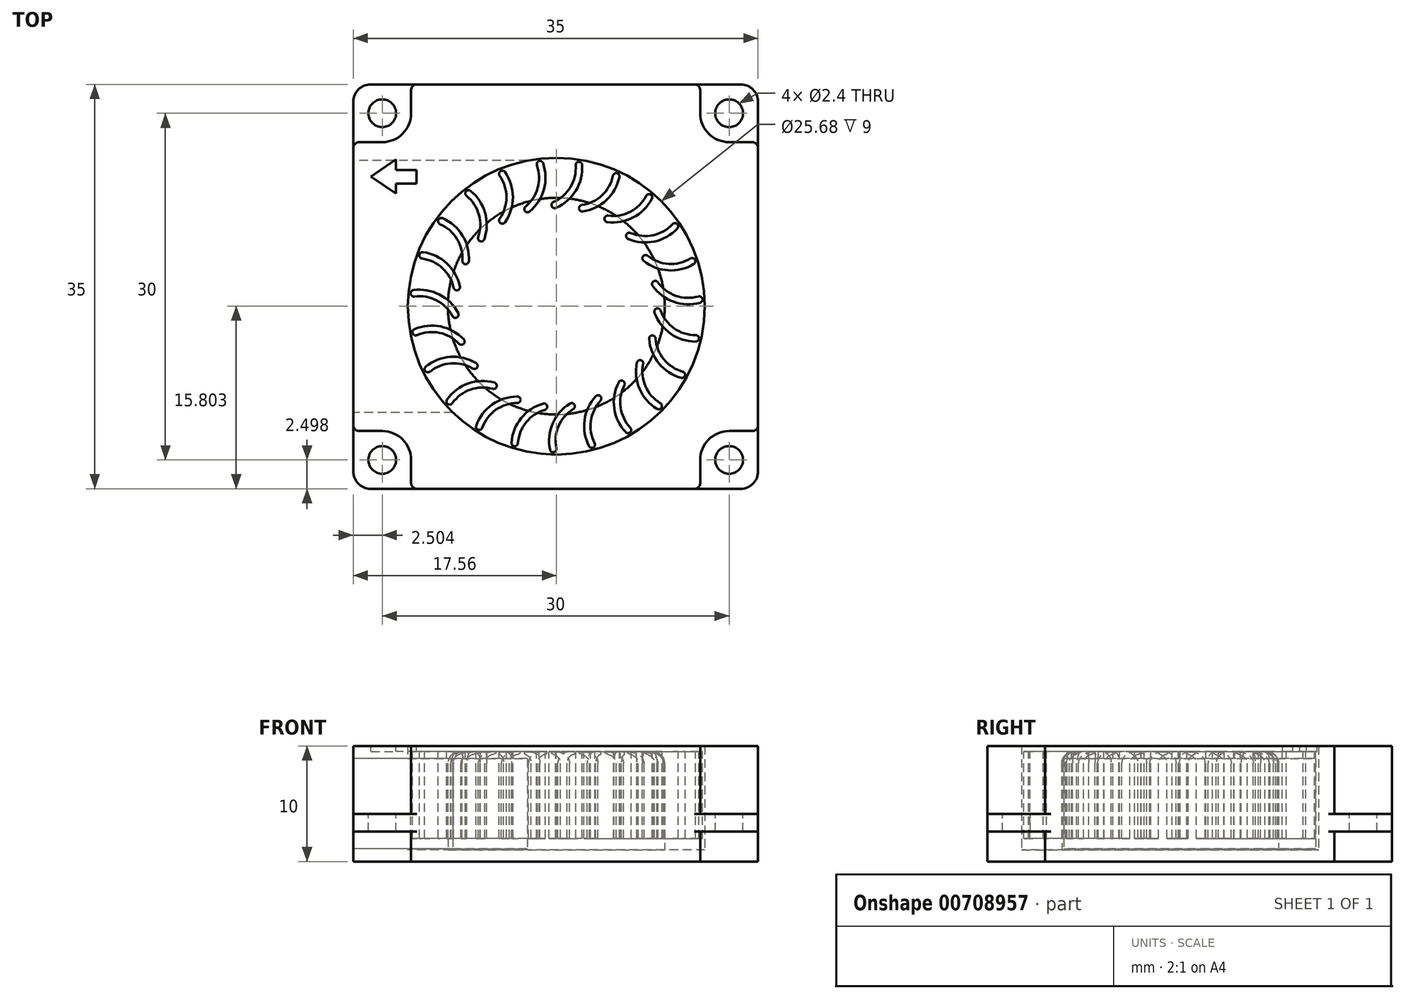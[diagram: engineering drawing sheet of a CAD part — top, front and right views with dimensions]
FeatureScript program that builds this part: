
annotation { "Feature Type Name" : "Feature", "Feature Type Description" : "" }
export const myFeature = defineFeature(function(context is Context, id is Id, definition is map)
    precondition{}
    {
        {
            var Q0;
            Q0=qCreatedBy(makeId("Top.planeOp"),FACE);
            var sketch = newSketch(context, id + "F0", { "sketchPlane" : qUnion([Q0])});
            skLineSegment(sketch, "E0.bottom", {"start": v(9.61, 18.92) * mm, "end": v(33.61, 18.92) * mm});
            skLineSegment(sketch, "E0.top", {"start": v(9.61, -16.08) * mm, "end": v(33.61, -16.08) * mm});
            skLineSegment(sketch, "E0.left", {"start": v(4.11, 13.42) * mm, "end": v(4.11, -10.58) * mm});
            skLineSegment(sketch, "E0.right", {"start": v(39.11, 13.42) * mm, "end": v(39.11, -10.58) * mm});
            skPoint(sketch, "E1.visualSharp", {"position": v(4.11, 18.92) * mm});
            skArc(sketch, "E1.filletArc", {"start": v(5.61, 18.92) * mm, "mid": v(4.55, 18.48) * mm, "end": v(4.11, 17.42) * mm});
            skPoint(sketch, "E2.visualSharp", {"position": v(39.11, 18.92) * mm});
            skArc(sketch, "E2.filletArc", {"start": v(39.11, 17.42) * mm, "mid": v(38.67, 18.48) * mm, "end": v(37.61, 18.92) * mm});
            skPoint(sketch, "E3.visualSharp", {"position": v(39.11, -16.08) * mm});
            skArc(sketch, "E3.filletArc", {"start": v(37.61, -16.08) * mm, "mid": v(38.67, -15.64) * mm, "end": v(39.11, -14.58) * mm});
            skPoint(sketch, "E4.visualSharp", {"position": v(4.11, -16.08) * mm});
            skArc(sketch, "E4.filletArc", {"start": v(4.11, -14.58) * mm, "mid": v(4.55, -15.64) * mm, "end": v(5.61, -16.08) * mm});
            skLineSegment(sketch, "E5", {"start": v(4.61, 13.92) * mm, "end": v(6.61, 13.92) * mm});
            skLineSegment(sketch, "E6", {"start": v(4.61, -11.08) * mm, "end": v(6.61, -11.08) * mm});
            skLineSegment(sketch, "E7", {"start": v(9.11, -15.58) * mm, "end": v(9.11, -13.58) * mm});
            skLineSegment(sketch, "E8", {"start": v(34.11, 18.42) * mm, "end": v(34.11, 16.42) * mm});
            skLineSegment(sketch, "E9.trimOffspring", {"start": v(36.61, 13.92) * mm, "end": v(38.61, 13.92) * mm});
            skLineSegment(sketch, "E10.trimOffspring", {"start": v(34.11, -13.58) * mm, "end": v(34.11, -15.58) * mm});
            skLineSegment(sketch, "E11.trimOffspring", {"start": v(36.61, -11.08) * mm, "end": v(38.61, -11.08) * mm});
            skLineSegment(sketch, "E12.trimOffspring", {"start": v(9.11, 16.42) * mm, "end": v(9.11, 18.42) * mm});
            skPoint(sketch, "E13.visualSharp", {"position": v(9.11, 13.92) * mm});
            skArc(sketch, "E13.filletArc", {"start": v(6.61, 13.92) * mm, "mid": v(8.38, 14.65) * mm, "end": v(9.11, 16.42) * mm});
            skPoint(sketch, "E14.visualSharp", {"position": v(34.11, 13.92) * mm});
            skArc(sketch, "E14.filletArc", {"start": v(34.11, 16.42) * mm, "mid": v(34.85, 14.65) * mm, "end": v(36.61, 13.92) * mm});
            skPoint(sketch, "E15.visualSharp", {"position": v(9.11, -11.08) * mm});
            skArc(sketch, "E15.filletArc", {"start": v(9.11, -13.58) * mm, "mid": v(8.38, -11.81) * mm, "end": v(6.61, -11.08) * mm});
            skPoint(sketch, "E16.visualSharp", {"position": v(34.11, -11.08) * mm});
            skArc(sketch, "E16.filletArc", {"start": v(36.61, -11.08) * mm, "mid": v(34.85, -11.81) * mm, "end": v(34.11, -13.58) * mm});
            skCircle(sketch, "E17", {"center": v(21.67, -0.28) * mm, "radius": 12.84 * mm});
            skPoint(sketch, "E18.newPointA", {"position": v(9.11, 18.92) * mm});
            skArc(sketch, "E18.filletArc", {"start": v(9.61, 18.92) * mm, "mid": v(9.26, 18.77) * mm, "end": v(9.11, 18.42) * mm});
            skPoint(sketch, "E19.newPointA", {"position": v(4.11, 13.92) * mm});
            skArc(sketch, "E19.filletArc", {"start": v(4.61, 13.92) * mm, "mid": v(4.26, 13.77) * mm, "end": v(4.11, 13.42) * mm});
            skPoint(sketch, "E20.newPointA", {"position": v(34.11, 18.92) * mm});
            skArc(sketch, "E20.filletArc", {"start": v(34.11, 18.42) * mm, "mid": v(33.97, 18.77) * mm, "end": v(33.61, 18.92) * mm});
            skPoint(sketch, "E21.newPointA", {"position": v(39.11, 13.92) * mm});
            skArc(sketch, "E21.filletArc", {"start": v(39.11, 13.42) * mm, "mid": v(38.97, 13.77) * mm, "end": v(38.61, 13.92) * mm});
            skArc(sketch, "E22.filletArc", {"start": v(38.61, -11.08) * mm, "mid": v(38.97, -10.94) * mm, "end": v(39.11, -10.58) * mm});
            skArc(sketch, "E23.filletArc", {"start": v(33.61, -16.08) * mm, "mid": v(33.97, -15.94) * mm, "end": v(34.11, -15.58) * mm});
            skPoint(sketch, "E24.newPointA", {"position": v(9.11, -16.08) * mm});
            skArc(sketch, "E24.filletArc", {"start": v(9.11, -15.58) * mm, "mid": v(9.26, -15.94) * mm, "end": v(9.61, -16.08) * mm});
            skPoint(sketch, "E25.newPointA", {"position": v(4.11, -11.08) * mm});
            skArc(sketch, "E25.filletArc", {"start": v(4.11, -10.58) * mm, "mid": v(4.26, -10.94) * mm, "end": v(4.61, -11.08) * mm});
            skLineSegment(sketch, "E26", {"start": v(4.11, -14.58) * mm, "end": v(4.11, -10.58) * mm});
            skLineSegment(sketch, "E27", {"start": v(5.61, -16.08) * mm, "end": v(9.61, -16.08) * mm});
            skLineSegment(sketch, "E28", {"start": v(33.61, -16.08) * mm, "end": v(37.61, -16.08) * mm});
            skLineSegment(sketch, "E29", {"start": v(39.11, -14.58) * mm, "end": v(39.11, -10.58) * mm});
            skLineSegment(sketch, "E30", {"start": v(39.11, 17.42) * mm, "end": v(39.11, 13.42) * mm});
            skLineSegment(sketch, "E31", {"start": v(37.61, 18.92) * mm, "end": v(33.61, 18.92) * mm});
            skLineSegment(sketch, "E32", {"start": v(9.61, 18.92) * mm, "end": v(5.61, 18.92) * mm});
            skLineSegment(sketch, "E33", {"start": v(4.11, 13.42) * mm, "end": v(4.11, 17.42) * mm});
            skSolve(sketch);
        }
        {
            var Q0;
            Q0=makeQuery(id+"F0.imprint","IMPRINT",FACE,{"disambiguationData":[TD([[makeQuery(id+"F0.imprint","IMPRINT",EDGE,{"derivedFrom":sQuery(id+"F0.wireOp",EDGE,"E0.bottom")}),-1.0]])]});
            extrude(context, id + "F1", {"entities" : qUnion([Q0]), "depth" : 10 * mm, "offsetDistance" : 25 * mm});
        }
        {
            var Q0;
            Q0=makeQuery(id+"F0.imprint","IMPRINT",FACE,{"disambiguationData":[TD([[makeQuery(id+"F0.imprint","IMPRINT",EDGE,{"derivedFrom":sQuery(id+"F0.wireOp",EDGE,"E17")}),1.0]])]});
            extrude(context, id + "F2", {"entities" : qUnion([Q0]), "operationType" : NewBodyOperationType.ADD, "depth" : 1 * mm, "offsetDistance" : 25 * mm});
        }
        {
            var Q0;
            Q0=makeQuery(id+"F0.imprint","IMPRINT",FACE,{"disambiguationData":[TD([[makeQuery(id+"F0.imprint","IMPRINT",EDGE,{"derivedFrom":sQuery(id+"F0.wireOp",EDGE,"E4.filletArc")}),1.0]])]});
            var Q1;
            Q1=makeQuery(id+"F0.imprint","IMPRINT",FACE,{"disambiguationData":[TD([[makeQuery(id+"F0.imprint","IMPRINT",EDGE,{"derivedFrom":sQuery(id+"F0.wireOp",EDGE,"E1.filletArc")}),1.0]])]});
            var Q2;
            Q2=makeQuery(id+"F0.imprint","IMPRINT",FACE,{"disambiguationData":[TD([[makeQuery(id+"F0.imprint","IMPRINT",EDGE,{"derivedFrom":sQuery(id+"F0.wireOp",EDGE,"E2.filletArc")}),1.0]])]});
            var Q3;
            Q3=makeQuery(id+"F0.imprint","IMPRINT",FACE,{"disambiguationData":[TD([[makeQuery(id+"F0.imprint","IMPRINT",EDGE,{"derivedFrom":sQuery(id+"F0.wireOp",EDGE,"E3.filletArc")}),1.0]])]});
            extrude(context, id + "F3", {"entities" : qUnion([Q0, Q1, Q2, Q3]), "operationType" : NewBodyOperationType.ADD, "depth" : 4.1 * mm, "offsetDistance" : 25 * mm, "hasSecondDirection" : true, "secondDirectionOppositeDirection" : false, "secondDirectionDepth" : 2.6 * mm});
        }
        {
            var Q0;
            Q0=makeQuery(id+"F3.opExtrude","CAP_FACE",FACE,{"disambiguationData":[OSD([sQuery(id+"F0.wireOp",EDGE,"E1.filletArc"),sQuery(id+"F0.wireOp",EDGE,"E5"),sQuery(id+"F0.wireOp",EDGE,"E12.trimOffspring"),sQuery(id+"F0.wireOp",EDGE,"E13.filletArc"),sQuery(id+"F0.wireOp",EDGE,"E18.filletArc"),sQuery(id+"F0.wireOp",EDGE,"E19.filletArc"),sQuery(id+"F0.wireOp",EDGE,"E32"),sQuery(id+"F0.wireOp",EDGE,"E33")])],"isStart":false});
            var sketch = newSketch(context, id + "F4", { "sketchPlane" : qUnion([Q0])});
            skLineSegment(sketch, "E34", {"start": v(4.11, 18.92) * mm, "end": v(39.11, -16.08) * mm, "construction": true});
            skLineSegment(sketch, "E35", {"start": v(39.11, -16.08) * mm, "end": v(39.11, 18.92) * mm, "construction": true});
            skLineSegment(sketch, "E36", {"start": v(39.11, 18.92) * mm, "end": v(4.11, -16.08) * mm, "construction": true});
            skPoint(sketch, "E37", {"position": v(6.61, 16.42) * mm});
            skPoint(sketch, "E38", {"position": v(36.61, 16.42) * mm});
            skPoint(sketch, "E39", {"position": v(6.61, -13.58) * mm});
            skPoint(sketch, "E40", {"position": v(36.61, -13.58) * mm});
            skSolve(sketch);
        }
        {
            var Q0;
            Q0=sQuery(id+"F4.wireOp",VERTEX,"E37");
            var Q1;
            Q1=sQuery(id+"F4.wireOp",VERTEX,"E39");
            var Q2;
            Q2=sQuery(id+"F4.wireOp",VERTEX,"E40");
            var Q3;
            Q3=sQuery(id+"F4.wireOp",VERTEX,"E38");
            var Q4;
            Q4=makeQuery(id+"F1.opExtrude","SWEPT_BODY",BODY,{"disambiguationData":[OSD([sQuery(id+"F0.wireOp",EDGE,"E0.bottom"),sQuery(id+"F0.wireOp",EDGE,"E0.top"),sQuery(id+"F0.wireOp",EDGE,"E0.left"),sQuery(id+"F0.wireOp",EDGE,"E0.right"),sQuery(id+"F0.wireOp",EDGE,"E5"),sQuery(id+"F0.wireOp",EDGE,"E6"),sQuery(id+"F0.wireOp",EDGE,"E7"),sQuery(id+"F0.wireOp",EDGE,"E8"),sQuery(id+"F0.wireOp",EDGE,"E9.trimOffspring"),sQuery(id+"F0.wireOp",EDGE,"E10.trimOffspring"),sQuery(id+"F0.wireOp",EDGE,"E11.trimOffspring"),sQuery(id+"F0.wireOp",EDGE,"E12.trimOffspring"),sQuery(id+"F0.wireOp",EDGE,"E13.filletArc"),sQuery(id+"F0.wireOp",EDGE,"E14.filletArc"),sQuery(id+"F0.wireOp",EDGE,"E15.filletArc"),sQuery(id+"F0.wireOp",EDGE,"E16.filletArc"),sQuery(id+"F0.wireOp",EDGE,"E17"),sQuery(id+"F0.wireOp",EDGE,"E18.filletArc"),sQuery(id+"F0.wireOp",EDGE,"E19.filletArc"),sQuery(id+"F0.wireOp",EDGE,"E20.filletArc"),sQuery(id+"F0.wireOp",EDGE,"E21.filletArc"),sQuery(id+"F0.wireOp",EDGE,"E22.filletArc"),sQuery(id+"F0.wireOp",EDGE,"E23.filletArc"),sQuery(id+"F0.wireOp",EDGE,"E24.filletArc"),sQuery(id+"F0.wireOp",EDGE,"E25.filletArc")])]});
            hole(context, id + "F5", {"style" : HoleStyle.C_BORE, "endStyle" : HoleEndStyle.BLIND, "holeDiameter" : 2.4 * mm, "cBoreDiameter" : 6.5 * mm, "cBoreDepth" : 0 * mm, "majorDiameter" : 5 * mm, "holeDepth" : 12 * mm, "isTappedThrough" : true, "tappedDepth" : 15 * mm, "tapClearance" : 0, "startFromSketch" : true, "locations" : qUnion([Q0, Q1, Q2, Q3]), "scope" : qUnion([Q4])});
        }
        {
            var Q0;
            Q0=makeQuery(id+"F3.boolean.opBoolean","MERGE",FACE,{"derivedFrom":[makeQuery(id+"F1.opExtrude","SWEPT_FACE",FACE,{"disambiguationData":[OSD([sQuery(id+"F0.wireOp",EDGE,"E0.left")])]}),makeQuery(id+"F3.opExtrude","SWEPT_FACE",FACE,{"disambiguationData":[OSD([sQuery(id+"F0.wireOp",EDGE,"E26")])]}),makeQuery(id+"F3.opExtrude","SWEPT_FACE",FACE,{"disambiguationData":[OSD([sQuery(id+"F0.wireOp",EDGE,"E33")])]})]});
            var sketch = newSketch(context, id + "F6", { "sketchPlane" : qUnion([Q0])});
            skLineSegment(sketch, "E41.bottom", {"start": v(-12.32, 8.9) * mm, "end": v(9.48, 8.9) * mm});
            skLineSegment(sketch, "E41.top", {"start": v(-12.32, 1.1) * mm, "end": v(9.48, 1.1) * mm});
            skLineSegment(sketch, "E41.left", {"start": v(-12.32, 8.9) * mm, "end": v(-12.32, 1.1) * mm});
            skLineSegment(sketch, "E41.right", {"start": v(9.48, 8.9) * mm, "end": v(9.48, 1.1) * mm});
            skLineSegment(sketch, "E42", {"start": v(-1.42, 8.9) * mm, "end": v(-1.42, 1.1) * mm, "construction": true});
            skSolve(sketch);
        }
        {
            var Q0;
            Q0=makeQuery(id+"F6.imprint","IMPRINT",FACE,{"disambiguationData":[TD([[makeQuery(id+"F6.imprint","IMPRINT",EDGE,{"derivedFrom":sQuery(id+"F6.wireOp",EDGE,"E41.bottom")}),-1.0]])]});
            extrude(context, id + "F7", {"entities" : qUnion([Q0]), "operationType" : NewBodyOperationType.REMOVE, "oppositeDirection" : true, "depth" : 18.2 * mm, "offsetDistance" : 25 * mm});
        }
        {
            var Q0;
            Q0=makeQuery(id+"F1.opExtrude","CAP_FACE",FACE,{"disambiguationData":[OSD([sQuery(id+"F0.wireOp",EDGE,"E0.bottom"),sQuery(id+"F0.wireOp",EDGE,"E0.top"),sQuery(id+"F0.wireOp",EDGE,"E0.left"),sQuery(id+"F0.wireOp",EDGE,"E0.right"),sQuery(id+"F0.wireOp",EDGE,"E5"),sQuery(id+"F0.wireOp",EDGE,"E6"),sQuery(id+"F0.wireOp",EDGE,"E7"),sQuery(id+"F0.wireOp",EDGE,"E8"),sQuery(id+"F0.wireOp",EDGE,"E9.trimOffspring"),sQuery(id+"F0.wireOp",EDGE,"E10.trimOffspring"),sQuery(id+"F0.wireOp",EDGE,"E11.trimOffspring"),sQuery(id+"F0.wireOp",EDGE,"E12.trimOffspring"),sQuery(id+"F0.wireOp",EDGE,"E13.filletArc"),sQuery(id+"F0.wireOp",EDGE,"E14.filletArc"),sQuery(id+"F0.wireOp",EDGE,"E15.filletArc"),sQuery(id+"F0.wireOp",EDGE,"E16.filletArc"),sQuery(id+"F0.wireOp",EDGE,"E17"),sQuery(id+"F0.wireOp",EDGE,"E18.filletArc"),sQuery(id+"F0.wireOp",EDGE,"E19.filletArc"),sQuery(id+"F0.wireOp",EDGE,"E20.filletArc"),sQuery(id+"F0.wireOp",EDGE,"E21.filletArc"),sQuery(id+"F0.wireOp",EDGE,"E22.filletArc"),sQuery(id+"F0.wireOp",EDGE,"E23.filletArc"),sQuery(id+"F0.wireOp",EDGE,"E24.filletArc"),sQuery(id+"F0.wireOp",EDGE,"E25.filletArc")])],"isStart":false});
            var sketch = newSketch(context, id + "F8", { "sketchPlane" : qUnion([Q0])});
            skLineSegment(sketch, "E43", {"start": v(5.65, 10.92) * mm, "end": v(7.8, 12.42) * mm});
            skLineSegment(sketch, "E44", {"start": v(7.8, 12.42) * mm, "end": v(7.8, 11.52) * mm});
            skLineSegment(sketch, "E45", {"start": v(7.8, 11.52) * mm, "end": v(9.6, 11.52) * mm});
            skLineSegment(sketch, "E46", {"start": v(9.6, 11.52) * mm, "end": v(9.6, 10.33) * mm});
            skLineSegment(sketch, "E47", {"start": v(9.6, 10.33) * mm, "end": v(7.8, 10.33) * mm});
            skLineSegment(sketch, "E48", {"start": v(7.8, 10.33) * mm, "end": v(7.8, 9.46) * mm});
            skLineSegment(sketch, "E49", {"start": v(7.8, 9.46) * mm, "end": v(5.65, 10.92) * mm});
            skLineSegment(sketch, "E50", {"start": v(5.65, 10.92) * mm, "end": v(9.6, 10.92) * mm});
            skSolve(sketch);
        }
        {
            var Q0;
            Q0=makeQuery(id+"F8.imprint","IMPRINT",FACE,{"disambiguationData":[TD([[makeQuery(id+"F8.imprint","IMPRINT",EDGE,{"derivedFrom":sQuery(id+"F8.wireOp",EDGE,"E43")}),-1.0]])]});
            var Q1;
            {var subQ0=sQuery(id+"F8.wireOp",EDGE,"E47");Q1=makeQuery(id+"F8.imprint","IMPRINT",FACE,{"disambiguationData":[TD([[makeQuery(id+"F8.imprint","IMPRINT",EDGE,{"derivedFrom":subQ0}),-1.0]])]});}
            extrude(context, id + "F9", {"entities" : qUnion([Q0, Q1]), "operationType" : NewBodyOperationType.REMOVE, "oppositeDirection" : true, "depth" : .5 * mm, "offsetDistance" : 25 * mm});
        }
        {
            var Q0;
            Q0=makeQuery(id+"F2.opExtrude","CAP_FACE",FACE,{"disambiguationData":[OSD([sQuery(id+"F0.wireOp",EDGE,"E17")])],"isStart":false});
            var sketch = newSketch(context, id + "F10", { "sketchPlane" : qUnion([Q0])});
            skCircle(sketch, "E51", {"center": v(21.67, -0.28) * mm, "radius": 9.38 * mm});
            skSolve(sketch);
        }
        {
            var Q0;
            Q0=makeQuery(id+"F10.imprint","IMPRINT",FACE,{"disambiguationData":[TD([[makeQuery(id+"F10.imprint","IMPRINT",EDGE,{"derivedFrom":sQuery(id+"F10.wireOp",EDGE,"E51")}),1.0]])]});
            var Q1;
            Q1=makeQuery(id+"F1.opExtrude","CAP_FACE",FACE,{"disambiguationData":[OSD([sQuery(id+"F0.wireOp",EDGE,"E0.bottom"),sQuery(id+"F0.wireOp",EDGE,"E0.top"),sQuery(id+"F0.wireOp",EDGE,"E0.left"),sQuery(id+"F0.wireOp",EDGE,"E0.right"),sQuery(id+"F0.wireOp",EDGE,"E5"),sQuery(id+"F0.wireOp",EDGE,"E6"),sQuery(id+"F0.wireOp",EDGE,"E7"),sQuery(id+"F0.wireOp",EDGE,"E8"),sQuery(id+"F0.wireOp",EDGE,"E9.trimOffspring"),sQuery(id+"F0.wireOp",EDGE,"E10.trimOffspring"),sQuery(id+"F0.wireOp",EDGE,"E11.trimOffspring"),sQuery(id+"F0.wireOp",EDGE,"E12.trimOffspring"),sQuery(id+"F0.wireOp",EDGE,"E13.filletArc"),sQuery(id+"F0.wireOp",EDGE,"E14.filletArc"),sQuery(id+"F0.wireOp",EDGE,"E15.filletArc"),sQuery(id+"F0.wireOp",EDGE,"E16.filletArc"),sQuery(id+"F0.wireOp",EDGE,"E17"),sQuery(id+"F0.wireOp",EDGE,"E18.filletArc"),sQuery(id+"F0.wireOp",EDGE,"E19.filletArc"),sQuery(id+"F0.wireOp",EDGE,"E20.filletArc"),sQuery(id+"F0.wireOp",EDGE,"E21.filletArc"),sQuery(id+"F0.wireOp",EDGE,"E22.filletArc"),sQuery(id+"F0.wireOp",EDGE,"E23.filletArc"),sQuery(id+"F0.wireOp",EDGE,"E24.filletArc"),sQuery(id+"F0.wireOp",EDGE,"E25.filletArc")])],"isStart":false});
            extrude(context, id + "F11", {"entities" : qUnion([Q0]), "operationType" : NewBodyOperationType.ADD, "endBound" : BoundingType.UP_TO_SURFACE, "depth" : 25 * mm, "endBoundEntityFace" : qUnion([Q1]), "hasOffset" : true, "offsetDistance" : .5 * mm});
        }
        {
            var Q0;
            Q0=makeQuery(id+"F11.opExtrude","CAP_EDGE",EDGE,{"disambiguationData":[OSD([sQuery(id+"F10.wireOp",EDGE,"E51")])],"isStart":false});
            fillet(context, id + "F12", {"entities" : qUnion([Q0]), "radius" : 1 * mm, "tangentPropagation" : true, "allowEdgeOverflow" : false});
        }
        {
            var Q0;
            Q0=makeQuery(id+"F11.opExtrude","CAP_FACE",FACE,{"disambiguationData":[OSD([sQuery(id+"F10.wireOp",EDGE,"E51")])],"isStart":false});
            var sketch = newSketch(context, id + "F13", { "sketchPlane" : qUnion([Q0])});
            skArc(sketch, "E52", {"start": v(21.42, 8.74) * mm, "mid": v(22.89, 10.03) * mm, "end": v(23.35, 11.92) * mm});
            skArc(sketch, "E53", {"start": v(21.65, 8.23) * mm, "mid": v(23.37, 9.74) * mm, "end": v(23.9, 11.96) * mm});
            skArc(sketch, "E54", {"start": v(23.9, 11.96) * mm, "mid": v(23.6, 12.22) * mm, "end": v(23.35, 11.92) * mm});
            skArc(sketch, "E55", {"start": v(21.42, 8.74) * mm, "mid": v(21.28, 8.38) * mm, "end": v(21.65, 8.23) * mm});
            skArc(sketch, "E56.1.0", {"start": v(19, 8.34) * mm, "mid": v(20.06, 9.97) * mm, "end": v(20, 11.92) * mm});
            skArc(sketch, "E56.1.1", {"start": v(19.35, 7.91) * mm, "mid": v(20.6, 9.83) * mm, "end": v(20.52, 12.1) * mm});
            skArc(sketch, "E56.1.2", {"start": v(19, 8.34) * mm, "mid": v(18.96, 7.95) * mm, "end": v(19.35, 7.91) * mm});
            skArc(sketch, "E56.1.3", {"start": v(20.52, 12.1) * mm, "mid": v(20.16, 12.28) * mm, "end": v(20, 11.92) * mm});
            skArc(sketch, "E56.2.0", {"start": v(16.77, 7.3) * mm, "mid": v(17.36, 9.16) * mm, "end": v(16.76, 11.02) * mm});
            skArc(sketch, "E56.2.1", {"start": v(17.23, 6.98) * mm, "mid": v(17.91, 9.16) * mm, "end": v(17.22, 11.34) * mm});
            skArc(sketch, "E56.2.2", {"start": v(16.77, 7.3) * mm, "mid": v(16.84, 6.91) * mm, "end": v(17.23, 6.98) * mm});
            skArc(sketch, "E56.2.3", {"start": v(17.22, 11.34) * mm, "mid": v(16.83, 11.4) * mm, "end": v(16.76, 11.02) * mm});
            skArc(sketch, "E56.3.0", {"start": v(14.91, 5.7) * mm, "mid": v(14.97, 7.65) * mm, "end": v(13.9, 9.27) * mm});
            skArc(sketch, "E56.3.1", {"start": v(15.44, 5.52) * mm, "mid": v(15.5, 7.8) * mm, "end": v(14.25, 9.7) * mm});
            skArc(sketch, "E56.3.2", {"start": v(14.91, 5.7) * mm, "mid": v(15.08, 5.34) * mm, "end": v(15.44, 5.52) * mm});
            skArc(sketch, "E56.3.3", {"start": v(14.25, 9.7) * mm, "mid": v(13.86, 9.67) * mm, "end": v(13.9, 9.27) * mm});
            skArc(sketch, "E56.4.0", {"start": v(13.55, 3.65) * mm, "mid": v(13.08, 5.55) * mm, "end": v(11.61, 6.82) * mm});
            skArc(sketch, "E56.4.1", {"start": v(14.1, 3.62) * mm, "mid": v(13.56, 5.84) * mm, "end": v(11.83, 7.34) * mm});
            skArc(sketch, "E56.4.2", {"start": v(13.55, 3.65) * mm, "mid": v(13.8, 3.36) * mm, "end": v(14.1, 3.62) * mm});
            skArc(sketch, "E56.4.3", {"start": v(11.83, 7.34) * mm, "mid": v(11.47, 7.19) * mm, "end": v(11.61, 6.82) * mm});
            skArc(sketch, "E56.5.0", {"start": v(12.79, 1.32) * mm, "mid": v(11.83, 3.01) * mm, "end": v(10.07, 3.85) * mm});
            skArc(sketch, "E56.5.1", {"start": v(13.33, 1.43) * mm, "mid": v(12.2, 3.42) * mm, "end": v(10.14, 4.4) * mm});
            skArc(sketch, "E56.5.2", {"start": v(12.79, 1.32) * mm, "mid": v(13.12, 1.1) * mm, "end": v(13.33, 1.43) * mm});
            skArc(sketch, "E56.5.3", {"start": v(10.14, 4.4) * mm, "mid": v(9.83, 4.16) * mm, "end": v(10.07, 3.85) * mm});
            skArc(sketch, "E56.6.0", {"start": v(12.69, -1.14) * mm, "mid": v(11.3, 0.24) * mm, "end": v(9.39, 0.56) * mm});
            skArc(sketch, "E56.6.1", {"start": v(13.18, -0.88) * mm, "mid": v(11.56, 0.73) * mm, "end": v(9.3, 1.12) * mm});
            skArc(sketch, "E56.6.2", {"start": v(12.69, -1.14) * mm, "mid": v(13.06, -1.25) * mm, "end": v(13.18, -0.88) * mm});
            skArc(sketch, "E56.6.3", {"start": v(9.3, 1.12) * mm, "mid": v(9.07, 0.8) * mm, "end": v(9.39, 0.56) * mm});
            skArc(sketch, "E56.7.0", {"start": v(13.25, -3.53) * mm, "mid": v(11.55, -2.58) * mm, "end": v(9.62, -2.78) * mm});
            skArc(sketch, "E56.7.1", {"start": v(13.66, -3.15) * mm, "mid": v(11.66, -2.03) * mm, "end": v(9.4, -2.27) * mm});
            skArc(sketch, "E56.7.2", {"start": v(13.25, -3.53) * mm, "mid": v(13.65, -3.54) * mm, "end": v(13.66, -3.15) * mm});
            skArc(sketch, "E56.7.3", {"start": v(9.4, -2.27) * mm, "mid": v(9.25, -2.64) * mm, "end": v(9.62, -2.78) * mm});
            skArc(sketch, "E56.8.0", {"start": v(14.44, -5.68) * mm, "mid": v(12.55, -5.22) * mm, "end": v(10.74, -5.94) * mm});
            skArc(sketch, "E56.8.1", {"start": v(14.73, -5.2) * mm, "mid": v(12.5, -4.67) * mm, "end": v(10.39, -5.5) * mm});
            skArc(sketch, "E56.8.2", {"start": v(14.44, -5.68) * mm, "mid": v(14.83, -5.58) * mm, "end": v(14.73, -5.2) * mm});
            skArc(sketch, "E56.8.3", {"start": v(10.39, -5.5) * mm, "mid": v(10.35, -5.9) * mm, "end": v(10.74, -5.94) * mm});
            skArc(sketch, "E56.9.0", {"start": v(16.17, -7.43) * mm, "mid": v(14.22, -7.5) * mm, "end": v(12.67, -8.68) * mm});
            skArc(sketch, "E56.9.1", {"start": v(16.32, -6.89) * mm, "mid": v(14.03, -6.98) * mm, "end": v(12.22, -8.36) * mm});
            skArc(sketch, "E56.9.2", {"start": v(16.17, -7.43) * mm, "mid": v(16.51, -7.23) * mm, "end": v(16.32, -6.89) * mm});
            skArc(sketch, "E56.9.3", {"start": v(12.22, -8.36) * mm, "mid": v(12.28, -8.75) * mm, "end": v(12.67, -8.68) * mm});
            skArc(sketch, "E56.10.0", {"start": v(18.3, -8.65) * mm, "mid": v(16.45, -9.24) * mm, "end": v(15.27, -10.8) * mm});
            skArc(sketch, "E56.10.1", {"start": v(18.3, -8.09) * mm, "mid": v(16.12, -8.79) * mm, "end": v(14.75, -10.61) * mm});
            skArc(sketch, "E56.10.2", {"start": v(18.3, -8.65) * mm, "mid": v(18.58, -8.37) * mm, "end": v(18.3, -8.09) * mm});
            skArc(sketch, "E56.10.3", {"start": v(14.75, -10.61) * mm, "mid": v(14.92, -10.97) * mm, "end": v(15.27, -10.8) * mm});
            skArc(sketch, "E56.11.0", {"start": v(20.69, -9.25) * mm, "mid": v(19.06, -10.32) * mm, "end": v(18.35, -12.13) * mm});
            skArc(sketch, "E56.11.1", {"start": v(20.53, -8.7) * mm, "mid": v(18.63, -9.97) * mm, "end": v(17.8, -12.1) * mm});
            skArc(sketch, "E56.11.2", {"start": v(20.69, -9.25) * mm, "mid": v(20.88, -8.9) * mm, "end": v(20.53, -8.7) * mm});
            skArc(sketch, "E56.11.3", {"start": v(17.8, -12.1) * mm, "mid": v(18.05, -12.4) * mm, "end": v(18.35, -12.13) * mm});
            skArc(sketch, "E56.12.0", {"start": v(23.14, -9.18) * mm, "mid": v(21.87, -10.65) * mm, "end": v(21.67, -12.59) * mm});
            skArc(sketch, "E56.12.1", {"start": v(22.85, -8.7) * mm, "mid": v(21.35, -10.43) * mm, "end": v(21.12, -12.7) * mm});
            skArc(sketch, "E56.12.2", {"start": v(23.14, -9.18) * mm, "mid": v(23.23, -8.8) * mm, "end": v(22.85, -8.7) * mm});
            skArc(sketch, "E56.12.3", {"start": v(21.12, -12.7) * mm, "mid": v(21.45, -12.92) * mm, "end": v(21.67, -12.59) * mm});
            skArc(sketch, "E56.13.0", {"start": v(25.49, -8.45) * mm, "mid": v(24.66, -10.21) * mm, "end": v(25, -12.13) * mm});
            skArc(sketch, "E56.13.1", {"start": v(25.08, -8.07) * mm, "mid": v(24.1, -10.14) * mm, "end": v(24.5, -12.39) * mm});
            skArc(sketch, "E56.13.2", {"start": v(25.49, -8.45) * mm, "mid": v(25.47, -8.06) * mm, "end": v(25.08, -8.07) * mm});
            skArc(sketch, "E56.13.3", {"start": v(24.5, -12.39) * mm, "mid": v(24.87, -12.5) * mm, "end": v(25, -12.13) * mm});
            skArc(sketch, "E56.14.0", {"start": v(27.55, -7.12) * mm, "mid": v(27.23, -9.04) * mm, "end": v(28.07, -10.8) * mm});
            skArc(sketch, "E56.14.1", {"start": v(27.06, -6.86) * mm, "mid": v(26.68, -9.12) * mm, "end": v(27.66, -11.18) * mm});
            skArc(sketch, "E56.14.2", {"start": v(27.55, -7.12) * mm, "mid": v(27.43, -6.74) * mm, "end": v(27.06, -6.86) * mm});
            skArc(sketch, "E56.14.3", {"start": v(27.66, -11.18) * mm, "mid": v(28.05, -11.2) * mm, "end": v(28.07, -10.8) * mm});
            skArc(sketch, "E56.15.0", {"start": v(29.18, -5.28) * mm, "mid": v(29.39, -7.21) * mm, "end": v(30.67, -8.68) * mm});
            skArc(sketch, "E56.15.1", {"start": v(28.63, -5.17) * mm, "mid": v(28.87, -7.44) * mm, "end": v(30.38, -9.16) * mm});
            skArc(sketch, "E56.15.2", {"start": v(29.18, -5.28) * mm, "mid": v(28.96, -4.95) * mm, "end": v(28.63, -5.17) * mm});
            skArc(sketch, "E56.15.3", {"start": v(30.38, -9.16) * mm, "mid": v(30.76, -9.06) * mm, "end": v(30.67, -8.68) * mm});
            skArc(sketch, "E56.16.0", {"start": v(30.25, -3.07) * mm, "mid": v(30.97, -4.87) * mm, "end": v(32.6, -5.94) * mm});
            skArc(sketch, "E56.16.1", {"start": v(29.7, -3.1) * mm, "mid": v(30.54, -5.23) * mm, "end": v(32.45, -6.48) * mm});
            skArc(sketch, "E56.16.2", {"start": v(30.25, -3.07) * mm, "mid": v(29.95, -2.8) * mm, "end": v(29.7, -3.1) * mm});
            skArc(sketch, "E56.16.3", {"start": v(32.45, -6.48) * mm, "mid": v(32.8, -6.28) * mm, "end": v(32.6, -5.94) * mm});
            skArc(sketch, "E56.17.0", {"start": v(30.68, -0.65) * mm, "mid": v(31.87, -2.2) * mm, "end": v(33.72, -2.78) * mm});
            skArc(sketch, "E56.17.1", {"start": v(30.16, -0.84) * mm, "mid": v(31.55, -2.65) * mm, "end": v(33.73, -3.34) * mm});
            skArc(sketch, "E56.17.2", {"start": v(30.68, -0.65) * mm, "mid": v(30.33, -0.48) * mm, "end": v(30.16, -0.84) * mm});
            skArc(sketch, "E56.17.3", {"start": v(33.73, -3.34) * mm, "mid": v(34, -3.06) * mm, "end": v(33.72, -2.78) * mm});
            skArc(sketch, "E56.18.0", {"start": v(30.45, 1.8) * mm, "mid": v(32, 0.63) * mm, "end": v(33.95, 0.56) * mm});
            skArc(sketch, "E56.18.1", {"start": v(30, 1.48) * mm, "mid": v(31.82, 0.1) * mm, "end": v(34.1, 0.03) * mm});
            skArc(sketch, "E56.18.2", {"start": v(30.45, 1.8) * mm, "mid": v(30.06, 1.86) * mm, "end": v(30, 1.48) * mm});
            skArc(sketch, "E56.18.3", {"start": v(34.1, 0.03) * mm, "mid": v(34.3, 0.37) * mm, "end": v(33.95, 0.56) * mm});
            skArc(sketch, "E56.19.0", {"start": v(29.56, 4.1) * mm, "mid": v(31.38, 3.38) * mm, "end": v(33.27, 3.85) * mm});
            skArc(sketch, "E56.19.1", {"start": v(29.21, 3.66) * mm, "mid": v(31.34, 2.83) * mm, "end": v(33.56, 3.37) * mm});
            skArc(sketch, "E56.19.2", {"start": v(29.56, 4.1) * mm, "mid": v(29.17, 4.05) * mm, "end": v(29.21, 3.66) * mm});
            skArc(sketch, "E56.19.3", {"start": v(33.56, 3.37) * mm, "mid": v(33.65, 3.75) * mm, "end": v(33.27, 3.85) * mm});
            skArc(sketch, "E56.20.0", {"start": v(28.1, 6.06) * mm, "mid": v(30.03, 5.87) * mm, "end": v(31.73, 6.82) * mm});
            skArc(sketch, "E56.20.1", {"start": v(27.87, 5.55) * mm, "mid": v(30.15, 5.32) * mm, "end": v(32.14, 6.44) * mm});
            skArc(sketch, "E56.20.2", {"start": v(28.1, 6.06) * mm, "mid": v(27.73, 5.91) * mm, "end": v(27.87, 5.55) * mm});
            skArc(sketch, "E56.20.3", {"start": v(32.14, 6.44) * mm, "mid": v(32.12, 6.84) * mm, "end": v(31.73, 6.82) * mm});
            skArc(sketch, "E56.21.0", {"start": v(26.15, 7.56) * mm, "mid": v(28.06, 7.9) * mm, "end": v(29.44, 9.27) * mm});
            skArc(sketch, "E56.21.1", {"start": v(26.07, 7) * mm, "mid": v(28.32, 7.4) * mm, "end": v(29.93, 9.02) * mm});
            skArc(sketch, "E56.21.2", {"start": v(26.15, 7.56) * mm, "mid": v(25.83, 7.32) * mm, "end": v(26.07, 7) * mm});
            skArc(sketch, "E56.21.3", {"start": v(29.93, 9.02) * mm, "mid": v(29.82, 9.4) * mm, "end": v(29.44, 9.27) * mm});
            skArc(sketch, "E56.22.0", {"start": v(23.87, 8.47) * mm, "mid": v(25.62, 9.32) * mm, "end": v(26.57, 11.02) * mm});
            skArc(sketch, "E56.22.1", {"start": v(23.94, 7.92) * mm, "mid": v(26, 8.91) * mm, "end": v(27.12, 10.9) * mm});
            skArc(sketch, "E56.22.2", {"start": v(23.87, 8.47) * mm, "mid": v(23.63, 8.16) * mm, "end": v(23.94, 7.92) * mm});
            skArc(sketch, "E56.22.3", {"start": v(27.12, 10.9) * mm, "mid": v(26.9, 11.23) * mm, "end": v(26.57, 11.02) * mm});
            skPoint(sketch, "E56.center", {"position": v(21.67, -0.28) * mm});
            skSolve(sketch);
        }
        {
            var Q0;
            Q0=makeQuery(id+"F13.imprint","IMPRINT",FACE,{"disambiguationData":[TD([[makeQuery(id+"F13.imprint","IMPRINT",EDGE,{"derivedFrom":sQuery(id+"F13.wireOp",EDGE,"E56.2.0")}),-1.0]])]});
            var Q1;
            Q1=makeQuery(id+"F13.imprint","IMPRINT",FACE,{"disambiguationData":[TD([[makeQuery(id+"F13.imprint","IMPRINT",EDGE,{"derivedFrom":sQuery(id+"F13.wireOp",EDGE,"E56.3.0")}),-1.0]])]});
            var Q2;
            Q2=makeQuery(id+"F13.imprint","IMPRINT",FACE,{"disambiguationData":[TD([[makeQuery(id+"F13.imprint","IMPRINT",EDGE,{"derivedFrom":sQuery(id+"F13.wireOp",EDGE,"E56.4.0")}),-1.0]])]});
            var Q3;
            Q3=makeQuery(id+"F13.imprint","IMPRINT",FACE,{"disambiguationData":[TD([[makeQuery(id+"F13.imprint","IMPRINT",EDGE,{"derivedFrom":sQuery(id+"F13.wireOp",EDGE,"E56.5.0")}),-1.0]])]});
            var Q4;
            Q4=makeQuery(id+"F13.imprint","IMPRINT",FACE,{"disambiguationData":[TD([[makeQuery(id+"F13.imprint","IMPRINT",EDGE,{"derivedFrom":sQuery(id+"F13.wireOp",EDGE,"E56.6.0")}),-1.0]])]});
            var Q5;
            Q5=makeQuery(id+"F13.imprint","IMPRINT",FACE,{"disambiguationData":[TD([[makeQuery(id+"F13.imprint","IMPRINT",EDGE,{"derivedFrom":sQuery(id+"F13.wireOp",EDGE,"E56.1.0")}),-1.0]])]});
            var Q6;
            Q6=makeQuery(id+"F13.imprint","IMPRINT",FACE,{"disambiguationData":[TD([[makeQuery(id+"F13.imprint","IMPRINT",EDGE,{"derivedFrom":sQuery(id+"F13.wireOp",EDGE,"E52")}),-1.0]])]});
            var Q7;
            Q7=makeQuery(id+"F13.imprint","IMPRINT",FACE,{"disambiguationData":[TD([[makeQuery(id+"F13.imprint","IMPRINT",EDGE,{"derivedFrom":sQuery(id+"F13.wireOp",EDGE,"E56.22.0")}),-1.0]])]});
            var Q8;
            Q8=makeQuery(id+"F13.imprint","IMPRINT",FACE,{"disambiguationData":[TD([[makeQuery(id+"F13.imprint","IMPRINT",EDGE,{"derivedFrom":sQuery(id+"F13.wireOp",EDGE,"E56.21.0")}),-1.0]])]});
            var Q9;
            Q9=makeQuery(id+"F13.imprint","IMPRINT",FACE,{"disambiguationData":[TD([[makeQuery(id+"F13.imprint","IMPRINT",EDGE,{"derivedFrom":sQuery(id+"F13.wireOp",EDGE,"E56.20.0")}),-1.0]])]});
            var Q10;
            Q10=makeQuery(id+"F13.imprint","IMPRINT",FACE,{"disambiguationData":[TD([[makeQuery(id+"F13.imprint","IMPRINT",EDGE,{"derivedFrom":sQuery(id+"F13.wireOp",EDGE,"E56.19.0")}),-1.0]])]});
            var Q11;
            Q11=makeQuery(id+"F13.imprint","IMPRINT",FACE,{"disambiguationData":[TD([[makeQuery(id+"F13.imprint","IMPRINT",EDGE,{"derivedFrom":sQuery(id+"F13.wireOp",EDGE,"E56.18.0")}),-1.0]])]});
            var Q12;
            Q12=makeQuery(id+"F13.imprint","IMPRINT",FACE,{"disambiguationData":[TD([[makeQuery(id+"F13.imprint","IMPRINT",EDGE,{"derivedFrom":sQuery(id+"F13.wireOp",EDGE,"E56.17.0")}),-1.0]])]});
            var Q13;
            Q13=makeQuery(id+"F13.imprint","IMPRINT",FACE,{"disambiguationData":[TD([[makeQuery(id+"F13.imprint","IMPRINT",EDGE,{"derivedFrom":sQuery(id+"F13.wireOp",EDGE,"E56.16.0")}),-1.0]])]});
            var Q14;
            Q14=makeQuery(id+"F13.imprint","IMPRINT",FACE,{"disambiguationData":[TD([[makeQuery(id+"F13.imprint","IMPRINT",EDGE,{"derivedFrom":sQuery(id+"F13.wireOp",EDGE,"E56.15.0")}),-1.0]])]});
            var Q15;
            Q15=makeQuery(id+"F13.imprint","IMPRINT",FACE,{"disambiguationData":[TD([[makeQuery(id+"F13.imprint","IMPRINT",EDGE,{"derivedFrom":sQuery(id+"F13.wireOp",EDGE,"E56.14.0")}),-1.0]])]});
            var Q16;
            Q16=makeQuery(id+"F13.imprint","IMPRINT",FACE,{"disambiguationData":[TD([[makeQuery(id+"F13.imprint","IMPRINT",EDGE,{"derivedFrom":sQuery(id+"F13.wireOp",EDGE,"E56.13.0")}),-1.0]])]});
            var Q17;
            Q17=makeQuery(id+"F13.imprint","IMPRINT",FACE,{"disambiguationData":[TD([[makeQuery(id+"F13.imprint","IMPRINT",EDGE,{"derivedFrom":sQuery(id+"F13.wireOp",EDGE,"E56.12.0")}),-1.0]])]});
            var Q18;
            Q18=makeQuery(id+"F13.imprint","IMPRINT",FACE,{"disambiguationData":[TD([[makeQuery(id+"F13.imprint","IMPRINT",EDGE,{"derivedFrom":sQuery(id+"F13.wireOp",EDGE,"E56.11.0")}),-1.0]])]});
            var Q19;
            Q19=makeQuery(id+"F13.imprint","IMPRINT",FACE,{"disambiguationData":[TD([[makeQuery(id+"F13.imprint","IMPRINT",EDGE,{"derivedFrom":sQuery(id+"F13.wireOp",EDGE,"E56.10.0")}),-1.0]])]});
            var Q20;
            Q20=makeQuery(id+"F13.imprint","IMPRINT",FACE,{"disambiguationData":[TD([[makeQuery(id+"F13.imprint","IMPRINT",EDGE,{"derivedFrom":sQuery(id+"F13.wireOp",EDGE,"E56.9.0")}),-1.0]])]});
            var Q21;
            Q21=makeQuery(id+"F13.imprint","IMPRINT",FACE,{"disambiguationData":[TD([[makeQuery(id+"F13.imprint","IMPRINT",EDGE,{"derivedFrom":sQuery(id+"F13.wireOp",EDGE,"E56.8.0")}),-1.0]])]});
            var Q22;
            Q22=makeQuery(id+"F13.imprint","IMPRINT",FACE,{"disambiguationData":[TD([[makeQuery(id+"F13.imprint","IMPRINT",EDGE,{"derivedFrom":sQuery(id+"F13.wireOp",EDGE,"E56.7.0")}),-1.0]])]});
            var Q23;
            Q23=makeQuery(id+"F2.opExtrude","CAP_FACE",FACE,{"disambiguationData":[OSD([sQuery(id+"F0.wireOp",EDGE,"E17")])],"isStart":false});
            extrude(context, id + "F14", {"entities" : qUnion([Q0, Q1, Q2, Q3, Q4, Q5, Q6, Q7, Q8, Q9, Q10, Q11, Q12, Q13, Q14, Q15, Q16, Q17, Q18, Q19, Q20, Q21, Q22]), "operationType" : NewBodyOperationType.ADD, "endBound" : BoundingType.UP_TO_SURFACE, "oppositeDirection" : true, "depth" : 25 * mm, "endBoundEntityFace" : qUnion([Q23]), "hasOffset" : true, "offsetDistance" : 1 * mm});
        }
    });
